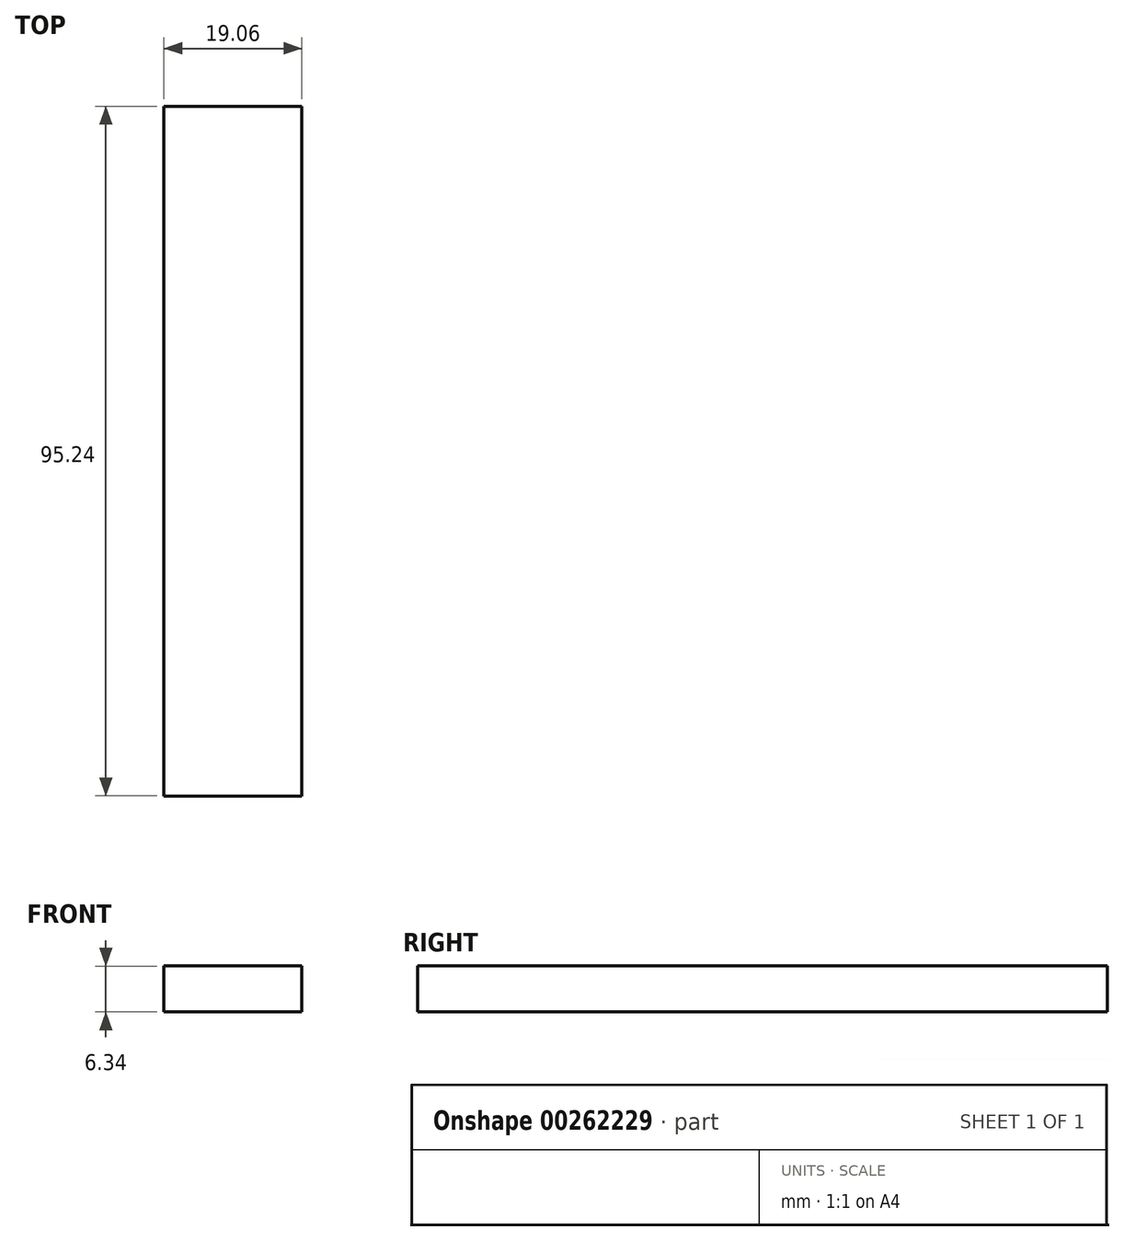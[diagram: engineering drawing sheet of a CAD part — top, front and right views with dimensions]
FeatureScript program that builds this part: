
annotation { "Feature Type Name" : "Feature", "Feature Type Description" : "" }
export const myFeature = defineFeature(function(context is Context, id is Id, definition is map)
    precondition{}
    {
        {
            var Q0;
            Q0=qCreatedBy(makeId("Front.planeOp"),FACE);
            var sketch = newSketch(context, id + "F0", { "sketchPlane" : qUnion([Q0])});
            skLineSegment(sketch, "E0.bottom", {"start": v(9.53, 3.18) * mm, "end": v(-9.53, 3.18) * mm});
            skLineSegment(sketch, "E0.top", {"start": v(9.52, -3.18) * mm, "end": v(-9.52, -3.18) * mm});
            skLineSegment(sketch, "E0.left", {"start": v(9.53, 3.18) * mm, "end": v(9.53, -3.17) * mm});
            skLineSegment(sketch, "E0.right", {"start": v(-9.53, 3.18) * mm, "end": v(-9.53, -3.17) * mm});
            skPoint(sketch, "E0.middle", {"position": v(0, 0) * mm});
            skSolve(sketch);
        }
        {
            var Q0;
            Q0 = qSketchRegion(id + "F0", true);
            extrude(context, id + "F1", {"entities" : qUnion([Q0]), "endBound" : BoundingType.SYMMETRIC, "depth" : 95.25 * mm});
        }
    });
